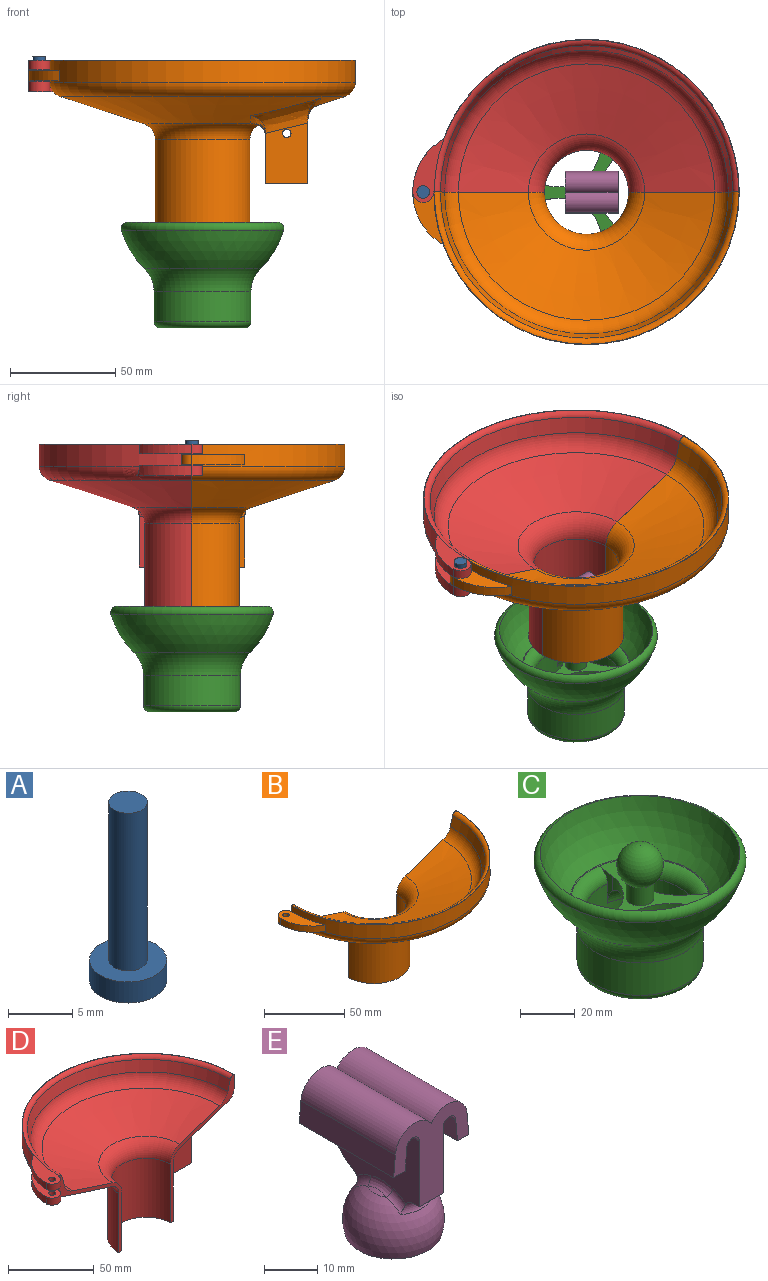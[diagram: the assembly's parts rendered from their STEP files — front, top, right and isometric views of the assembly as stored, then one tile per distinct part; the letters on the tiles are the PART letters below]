
ASSEMBLY  parts=5 mates=4
PART A: 5 faces, bbox 6x6x17 mm
  f0: cylinder r=1.5mm len=15mm, axis (0,0,-1), area 141.4mm2, adj f1,f4
  f1: plane 3x3mm, normal (0,0,1), area 7.1mm2, adj f0
  f2: cylinder r=3mm len=6mm, axis (0,0,1), area 37.7mm2, adj f3,f4
  f3: plane 6x6mm, normal (0,0,-1), area 28.3mm2, adj f2
  f4: plane 6x6mm, normal (0,0,1), area 21.2mm2, adj f0,f2
PART B: 32 faces, bbox 163.3x89.4x80.2 mm
  f0: plane 24.11x12.77mm, normal (-1,0,0), area 291.7mm2, adj f22,f23,f25,f26,f29,f30
  f1: cone r=22.5mm half-angle=71.9deg, axis (0,0,1), area 5078.5mm2, adj f9,f10,f12,f18,f26,f28,f30
  f2: cylinder r=72.5mm len=145mm, axis (0,0,-1), area 2253.2mm2, adj f6,f9,f10,f14,f16,f17,f18
  f3: cylinder r=20mm len=42.02mm, axis (0,0,-1), area 2640mm2, adj f8,f9,f10,f11
  f4: cone r=66mm half-angle=71.9deg, axis (0,0,1), area 4857.4mm2, adj f9,f10,f11,f19
  f5: cone r=70mm half-angle=14.9deg, axis (0,0,1), area 1673.8mm2, adj f9,f10,f19,f20
  f6: plane 145x72.5mm, normal (0,0,1), area 44.4mm2, adj f2,f9,f10,f20
  f7: cylinder r=22.5mm len=45mm, axis (0,0,-1), area 2995.6mm2, adj f8,f9,f10,f12
  f8: plane 45x22.5mm, normal (0,0,-1), area 166.9mm2, adj f3,f7,f9,f10
  f9: plane 80x52.5mm, normal (0,1,0), area 311.3mm2, adj f1,f2,f3,f4,f5,f6,f7,f8
  f10: plane 80x52.5mm, normal (0,1,0), area 311.3mm2, adj f1,f2,f3,f4,f5,f6,f7,f8
  f11: torus R=31mm, axis (0,0,1), area 983.7mm2, adj f3,f4,f9,f10
  f12: torus R=30.5mm, axis (0,0,-1), area 771.3mm2, adj f1,f7,f9,f10,f29
  f13: cylinder r=5mm len=10mm, axis (0,0,1), area 75.4mm2, adj f10,f14,f16,f17
  f14: cylinder r=28.82mm len=24.98mm, axis (0,0,1), area 145mm2, adj f2,f13,f16,f17
  f15: cylinder r=2mm len=4.8mm, axis (0,0,1), area 60.3mm2, adj f16,f17
  f16: plane 29.98x14.44mm, normal (0,0,-1), area 208.1mm2, adj f2,f13,f14,f15
  f17: plane 29.98x14.44mm, normal (0,0,1), area 208.1mm2, adj f2,f13,f14,f15
  f18: torus R=65.5mm, axis (0,0,1), area 1954.9mm2, adj f1,f2,f9,f10
  f19: torus R=57.74mm, axis (0,0,-1), area 2022.5mm2, adj f4,f5,f9,f10
  f20: torus R=72.3mm, axis (0,0,1), area 871.9mm2, adj f5,f6,f9,f10
  f21: plane 31.41x13.21mm, normal (1,0,0), area 390.5mm2, adj f22,f23,f25,f26,f28
  f22: plane 20x12.75mm, normal (0,0,-1), area 255mm2, adj f0,f21,f23,f25
  f23: plane 28.5x20.01mm, normal (0,-1,0), area 506.9mm2, adj f0,f21,f22,f26,f31
  f24: plane 28.38x9.42mm, normal (0.31,0,-0.95), area 206mm2, adj f9,f27,f28,f29
  f25: plane 30.18x20.15mm, normal (0,1,0), area 525.5mm2, adj f0,f21,f22,f27,f28,f29,f31
  f26: bspline ~47x20.41mm, area 343.4mm2, adj f0,f1,f21,f23,f28,f30
  f27: cylinder r=5mm len=28.29mm, axis (0.95,0,0.31), area 193.6mm2, adj f24,f25,f28,f29
  f28: bspline ~51.7x12.26mm, area 195.8mm2, adj f1,f21,f24,f25,f26,f27
  f29: bspline ~19.55x8.67mm, area 57.6mm2, adj f0,f12,f24,f25,f27,f30
  f30: bspline ~27.49x13.17mm, area 126.6mm2, adj f0,f1,f26,f29
  f31: cylinder r=2mm len=12.75mm, axis (0,1,0), area 160.2mm2, adj f23,f25
PART C: 27 faces, bbox 83.6x83.6x53.5 mm
  f0: plane 46.24x44.69mm, normal (0,0,1), area 420.3mm2, adj f3,f8,f9,f10,f11,f12,f13,f14
  f1: plane 19.1x18.51mm, normal (0,0,-1), area 205.5mm2, adj f9,f11,f15,f17,f18,f19
  f2: sphere r=8.5mm, area 821.1mm2, adj f3
  f3: cylinder r=5mm len=10mm, axis (0,0,1), area 251.3mm2, adj f0,f2
  f4: sphere r=37.08mm, area 4613.2mm2, adj f21,f26
  f5: sphere r=40.02mm, area 4540mm2, adj f20,f21
  f6: cylinder r=23mm len=46mm, axis (0,0,1), area 2087mm2, adj f20,f22
  f7: cylinder r=20mm len=40mm, axis (0,0,1), area 2966.3mm2, adj f8,f10,f12,f13,f14,f16,f17,f18
  f8: plane 13.63x7.3mm, normal (0.88,-0.48,0), area 33.1mm2, adj f0,f7,f9,f19,f25
  f9: cylinder r=20mm len=25.21mm, axis (0,0,-1), area 112.6mm2, adj f0,f1,f8,f10,f17,f19
  f10: plane 13.63x6.49mm, normal (0.62,0.78,0), area 33.1mm2, adj f0,f7,f9,f17,f25
  f11: cylinder r=20mm len=24.36mm, axis (0,0,-1), area 112.6mm2, adj f0,f1,f12,f13,f17,f18
  f12: plane 13.63x7.74mm, normal (0.36,-0.93,0), area 33.1mm2, adj f0,f7,f11,f18,f24
  f13: plane 13.63x7.1mm, normal (-0.85,-0.52,0), area 33.1mm2, adj f0,f7,f11,f17,f24
  f14: plane 13.63x8.31mm, normal (-0.02,1,0), area 33.1mm2, adj f0,f7,f15,f18,f23
  f15: cylinder r=20mm len=19.3mm, axis (0,0,-1), area 112.6mm2, adj f0,f1,f14,f16,f18,f19
  f16: plane 13.63x8.22mm, normal (-0.99,0.15,0), area 33.1mm2, adj f0,f7,f15,f19,f23
  f17: torus R=10mm, axis (0,0,1), area 95.2mm2, adj f1,f7,f9,f10,f11,f13
  f18: torus R=10mm, axis (0,0,1), area 95.2mm2, adj f1,f7,f11,f12,f14,f15
  f19: torus R=10mm, axis (0,0,1), area 95.2mm2, adj f1,f7,f8,f9,f15,f16
  f20: torus R=38mm, axis (0,0,1), area 1873mm2, adj f5,f6
  f21: torus R=35.63mm, axis (0,0,-1), area 1140.5mm2, adj f4,f5
  f22: torus R=20mm, axis (0,0,1), area 648.7mm2, adj f6,f7
  f23: torus R=25.1mm, axis (0,0,-1), area 305.3mm2, adj f7,f14,f16,f26
  f24: torus R=25.1mm, axis (0,0,-1), area 305.3mm2, adj f7,f12,f13,f26
  f25: torus R=25.1mm, axis (0,0,-1), area 305.3mm2, adj f7,f8,f10,f26
  f26: torus R=25.09mm, axis (0,0,-1), area 60mm2, adj f0,f4,f23,f24,f25
PART D: 36 faces, bbox 163.3x89.4x80.2 mm
  f0: plane 24.11x12.77mm, normal (-1,0,0), area 291.7mm2, adj f26,f27,f29,f30,f33,f34
  f1: cone r=22.5mm half-angle=71.9deg, axis (0,0,1), area 5078.5mm2, adj f9,f10,f12,f22,f30,f32,f34
  f2: cylinder r=72.5mm len=145mm, axis (0,0,1), area 2249.8mm2, adj f6,f9,f10,f13,f16,f17,f21,f22
  f3: cylinder r=20mm len=42.02mm, axis (0,0,1), area 2640mm2, adj f8,f9,f10,f11
  f4: cone r=66mm half-angle=71.9deg, axis (0,0,1), area 4857.4mm2, adj f9,f10,f11,f23
  f5: cone r=70mm half-angle=14.9deg, axis (0,0,1), area 1673.8mm2, adj f9,f10,f23,f24
  f6: plane 155x77.5mm, normal (0,0,1), area 252.5mm2, adj f2,f9,f10,f13,f14,f15,f24
  f7: cylinder r=22.5mm len=45mm, axis (0,0,1), area 2995.6mm2, adj f8,f9,f10,f12
  f8: plane 45x22.5mm, normal (0,0,-1), area 166.9mm2, adj f3,f7,f9,f10
  f9: plane 80x52.5mm, normal (0,-1,0), area 311.3mm2, adj f1,f2,f3,f4,f5,f6,f7,f8
  f10: plane 80x52.5mm, normal (0,-1,0), area 313.7mm2, adj f1,f2,f3,f4,f5,f6,f7,f8
  f11: torus R=31mm, axis (0,0,-1), area 983.7mm2, adj f3,f4,f9,f10
  f12: torus R=30.5mm, axis (0,0,1), area 771.3mm2, adj f1,f7,f9,f10,f33
  f13: cylinder r=28.82mm len=24.98mm, axis (0,0,1), area 136mm2, adj f2,f6,f14,f16
  f14: cylinder r=5mm len=10mm, axis (0,0,1), area 70.7mm2, adj f6,f10,f13,f16
  f15: cylinder r=2mm len=4.5mm, axis (0,0,1), area 56.5mm2, adj f6,f16
  f16: plane 29.98x14.44mm, normal (0,0,-1), area 208.1mm2, adj f2,f13,f14,f15
  f17: cylinder r=28.82mm len=26.15mm, axis (0,0,1), area 154.8mm2, adj f2,f18,f20,f21,f22
  f18: cylinder r=5mm len=10mm, axis (0,0,1), area 78.5mm2, adj f10,f17,f20,f21
  f19: cylinder r=2mm len=5mm, axis (0,0,1), area 62.8mm2, adj f20,f21
  f20: plane 31.15x16.71mm, normal (0,0,-1), area 252.6mm2, adj f10,f17,f18,f19,f22
  f21: plane 29.98x14.44mm, normal (0,0,1), area 208.1mm2, adj f2,f17,f18,f19
  f22: torus R=65.5mm, axis (0,0,-1), area 1824.2mm2, adj f1,f2,f9,f10,f17,f20
  f23: torus R=57.74mm, axis (0,0,1), area 2022.5mm2, adj f4,f5,f9,f10
  f24: torus R=72.3mm, axis (0,0,-1), area 871.9mm2, adj f5,f6,f9,f10
  f25: plane 31.41x13.21mm, normal (1,0,0), area 390.5mm2, adj f26,f27,f29,f30,f32
  f26: plane 20x12.75mm, normal (0,0,-1), area 255mm2, adj f0,f25,f27,f29
  f27: plane 28.5x20.01mm, normal (0,1,0), area 506.9mm2, adj f0,f25,f26,f30,f35
  f28: plane 28.38x9.42mm, normal (0.31,0,-0.95), area 206mm2, adj f9,f31,f32,f33
  f29: plane 30.18x20.15mm, normal (0,-1,0), area 525.5mm2, adj f0,f25,f26,f31,f32,f33,f35
  f30: bspline ~47x20.41mm, area 343.4mm2, adj f0,f1,f25,f27,f32,f34
  f31: cylinder r=5mm len=28.29mm, axis (-0.95,0,-0.31), area 193.6mm2, adj f28,f29,f32,f33
  f32: bspline ~51.7x12.26mm, area 195.8mm2, adj f1,f25,f28,f29,f30,f31
  f33: bspline ~20.97x8.67mm, area 57.6mm2, adj f0,f12,f28,f29,f31,f34
  f34: bspline ~27.49x13.18mm, area 126.6mm2, adj f0,f1,f30,f33
  f35: cylinder r=2mm len=12.75mm, axis (0,-1,0), area 160.2mm2, adj f27,f29
PART E: 32 faces, bbox 22.3x28.7x34.3 mm
  f0: plane 27.39x18.54mm, normal (-1,0,0), area 343.7mm2, adj f1,f7,f18,f19,f21,f22,f23,f24
  f1: plane 19.87x9.74mm, normal (0,1,0), area 112.3mm2, adj f0,f8,f9,f10,f11,f12,f13,f14
  f2: cone r=4.98mm half-angle=58.5deg, axis (0,0,-1), area 0mm2, adj f5,f27
  f3: sphere r=8.55mm, area 586.2mm2, adj f20
  f4: plane 18.13x18.13mm, normal (0,0,-1), area 20.6mm2, adj f5,f20
  f5: sphere r=9.55mm, area 600.2mm2, adj f2,f4,f6,f21,f23,f24,f25,f26
  f6: cone r=4.98mm half-angle=58.5deg, axis (0,0,-1), area 0mm2, adj f5,f22
  f7: plane 6.37x1.52mm, normal (0,0,-1), area 7.2mm2, adj f0,f8,f19,f23
  f8: plane 27.35x18.5mm, normal (1,0,0), area 343.7mm2, adj f1,f7,f9,f19,f23,f25,f26,f27
  f9: cylinder r=1.66mm len=25mm, axis (0,1,0), area 130.2mm2, adj f1,f8,f10,f19
  f10: plane 25x4.98mm, normal (-1,0,-0.09), area 125mm2, adj f1,f9,f11,f19
  f11: plane 25x3mm, normal (0,0,-1), area 75mm2, adj f1,f10,f12,f19
  f12: plane 25x4.98mm, normal (1,0,0.09), area 125mm2, adj f1,f11,f13,f19
  f13: cylinder r=5.21mm len=25mm, axis (0,1,0), area 320.2mm2, adj f1,f12,f14,f19
  f14: cylinder r=5.21mm len=25mm, axis (0,1,0), area 320.2mm2, adj f1,f13,f15,f19
  f15: plane 25x4.98mm, normal (-1,0,0.09), area 125mm2, adj f1,f14,f16,f19
  f16: plane 25x3mm, normal (0,0,-1), area 75mm2, adj f1,f15,f17,f19
  f17: plane 25x4.98mm, normal (1,0,-0.09), area 125mm2, adj f1,f16,f18,f19
  f18: cylinder r=1.66mm len=25mm, axis (0,1,0), area 130.2mm2, adj f0,f1,f17,f19
  f19: plane 19.87x19.76mm, normal (0,-1,0), area 189.9mm2, adj f0,f7,f8,f9,f10,f11,f12,f13
  f20: torus R=8.7mm, axis (0,0,-1), area 48.6mm2, adj f3,f4
  f21: torus R=10.32mm, axis (-1,0,0), area 9mm2, adj f0,f5,f22,f23
  f22: bspline ~8.15x2.75mm, area 12mm2, adj f0,f6,f21,f24
  f23: torus R=9.06mm, axis (0,0,-1), area 31.7mm2, adj f0,f5,f7,f8,f21,f25
  f24: torus R=10.32mm, axis (-1,0,0), area 9mm2, adj f0,f5,f22,f26
  f25: torus R=10.32mm, axis (-1,0,0), area 9mm2, adj f5,f8,f23,f27
  f26: torus R=9.06mm, axis (0,0,1), area 24.8mm2, adj f0,f5,f8,f24,f28,f30
  f27: bspline ~8.15x2.75mm, area 12mm2, adj f2,f8,f25,f28
  f28: torus R=10.32mm, axis (-1,0,0), area 9mm2, adj f5,f8,f26,f27
  f29: plane 6.37x2.26mm, normal (0,0.87,-0.49), area 12.9mm2, adj f0,f8,f30,f31
  f30: bspline ~14.13x8.4mm, area 51.3mm2, adj f0,f8,f26,f29
  f31: cylinder r=12mm len=6.37mm, axis (-1,0,0), area 39.1mm2, adj f0,f1,f8,f29
PLACE A rot(axis=(1,0,0),180deg) t=(18.31,108.35,3.6)mm
PLACE B t=(95.81,108.35,3.55)mm
PLACE C rot(axis=(0,0,-1),11deg) t=(95.81,108.35,-78.45)mm
PLACE D t=(95.81,108.35,3.6)mm
PLACE E rot(axis=(0,0,-1),90deg) t=(95.81,108.35,-78.45)mm
MATE fastened E.f23 <-> B.f1  axis (0,0,1) through (95.81,108.35,-78.45)mm
MATE revolute D.f14 <-> A.f0  axis (0,0,1) through (18.31,108.35,3.6)mm
MATE revolute B.f15 <-> A.f2  axis (0,0,1) through (18.31,108.35,-1.25)mm
MATE ball C.f3 <-> E.f20  axis (0,0,1) through (95.81,108.35,-78.45)mm
